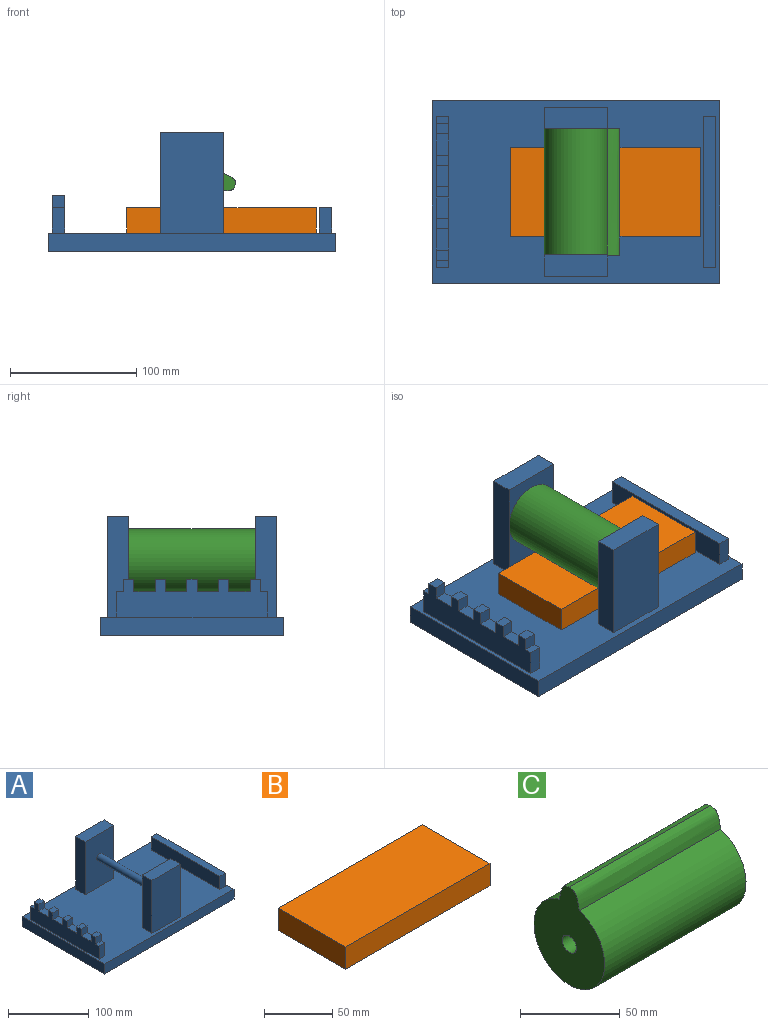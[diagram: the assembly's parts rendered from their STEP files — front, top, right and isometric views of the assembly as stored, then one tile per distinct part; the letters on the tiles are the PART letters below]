
ASSEMBLY  parts=3 mates=2
PART A: 47 faces, bbox 227.5x144.3x95 mm
  f0: plane 17x10mm, normal (0,0,1), area 170mm2, adj f17,f19,f41,f45
  f1: plane 17x10mm, normal (0,0,1), area 170mm2, adj f17,f19,f38,f42
  f2: plane 17x10mm, normal (0,0,1), area 170mm2, adj f17,f19,f35,f39
  f3: plane 17x10mm, normal (0,0,1), area 170mm2, adj f17,f19,f32,f36
  f4: plane 10x6mm, normal (0,0,1), area 60mm2, adj f16,f17,f19,f33
  f5: plane 227.5x144.3mm, normal (0,0,1), area 28729mm2, adj f6,f7,f8,f9,f11,f12,f13,f14
  f6: plane 144.3x15mm, normal (1,0,0), area 2164.5mm2, adj f5,f7,f9,f10
  f7: plane 227.5x15mm, normal (0,-1,0), area 3412.5mm2, adj f5,f6,f8,f10
  f8: plane 144.3x15mm, normal (-1,0,0), area 2164.5mm2, adj f5,f7,f9,f10
  f9: plane 227.5x15mm, normal (0,1,0), area 3412.5mm2, adj f5,f6,f8,f10
  f10: plane 227.5x144.3mm, normal (0,0,-1), area 32829mm2, adj f6,f7,f8,f9
  f11: plane 20x10mm, normal (0,-1,0), area 200mm2, adj f5,f12,f14,f15
  f12: plane 120x20mm, normal (1,0,0), area 2400mm2, adj f5,f11,f13,f15
  f13: plane 20x10mm, normal (0,1,0), area 200mm2, adj f5,f12,f14,f15
  f14: plane 120x20mm, normal (-1,0,0), area 2400mm2, adj f5,f11,f13,f15
  f15: plane 120x10mm, normal (0,0,1), area 1200mm2, adj f11,f12,f13,f14
  f16: plane 20x10mm, normal (0,1,0), area 200mm2, adj f4,f5,f17,f19
  f17: plane 120x30mm, normal (-1,0,0), area 2800mm2, adj f0,f1,f2,f3,f4,f5,f16,f18
  f18: plane 20x10mm, normal (0,-1,0), area 200mm2, adj f5,f17,f19,f20
  f19: plane 120x30mm, normal (1,0,0), area 2800mm2, adj f0,f1,f2,f3,f4,f5,f16,f18
  f20: plane 10x6mm, normal (0,0,1), area 60mm2, adj f17,f18,f19,f44
  f21: plane 80x50mm, normal (0,1,0), area 4000mm2, adj f5,f22,f24,f25
  f22: plane 80x17mm, normal (-1,0,0), area 1360mm2, adj f5,f21,f23,f25
  f23: plane 80x50mm, normal (0,-1,0), area 3921.5mm2, adj f5,f22,f24,f25,f26
  f24: plane 80x17mm, normal (1,0,0), area 1360mm2, adj f5,f21,f23,f25
  f25: plane 50x17mm, normal (0,0,1), area 850mm2, adj f21,f22,f23,f24
  f26: cylinder r=5mm len=100mm, axis (0,-1,0), area 3141.6mm2, adj f23,f30
  f27: plane 80x17mm, normal (-1,0,0), area 1360mm2, adj f5,f28,f30,f31
  f28: plane 80x50mm, normal (0,-1,0), area 4000mm2, adj f5,f27,f29,f31
  f29: plane 80x17mm, normal (1,0,0), area 1360mm2, adj f5,f28,f30,f31
  f30: plane 80x50mm, normal (0,1,0), area 3921.5mm2, adj f5,f26,f27,f29,f31
  f31: plane 50x17mm, normal (0,0,1), area 850mm2, adj f27,f28,f29,f30
  f32: plane 10x10mm, normal (0,-1,0), area 100mm2, adj f3,f17,f19,f34
  f33: plane 10x10mm, normal (0,1,0), area 100mm2, adj f4,f17,f19,f34
  f34: plane 10x8mm, normal (0,0,1), area 80mm2, adj f17,f19,f32,f33
  f35: plane 10x10mm, normal (0,-1,0), area 100mm2, adj f2,f17,f19,f37
  f36: plane 10x10mm, normal (0,1,0), area 100mm2, adj f3,f17,f19,f37
  f37: plane 10x8mm, normal (0,0,1), area 80mm2, adj f17,f19,f35,f36
  f38: plane 10x10mm, normal (0,-1,0), area 100mm2, adj f1,f17,f19,f40
  f39: plane 10x10mm, normal (0,1,0), area 100mm2, adj f2,f17,f19,f40
  f40: plane 10x8mm, normal (0,0,1), area 80mm2, adj f17,f19,f38,f39
  f41: plane 10x10mm, normal (0,-1,0), area 100mm2, adj f0,f17,f19,f43
  f42: plane 10x10mm, normal (0,1,0), area 100mm2, adj f1,f17,f19,f43
  f43: plane 10x8mm, normal (0,0,1), area 80mm2, adj f17,f19,f41,f42
  f44: plane 10x10mm, normal (0,-1,0), area 100mm2, adj f17,f19,f20,f46
  f45: plane 10x10mm, normal (0,1,0), area 100mm2, adj f0,f17,f19,f46
  f46: plane 10x8mm, normal (0,0,1), area 80mm2, adj f17,f19,f44,f45
PART B: 6 faces, bbox 150x70x20 mm
  f0: plane 70x20mm, normal (1,0,0), area 1400mm2, adj f1,f3,f4,f5
  f1: plane 150x20mm, normal (0,1,0), area 3000mm2, adj f0,f2,f4,f5
  f2: plane 70x20mm, normal (-1,0,0), area 1400mm2, adj f1,f3,f4,f5
  f3: plane 150x20mm, normal (0,-1,0), area 3000mm2, adj f0,f2,f4,f5
  f4: plane 150x70mm, normal (0,0,1), area 10500mm2, adj f0,f1,f2,f3
  f5: plane 150x70mm, normal (0,0,-1), area 10500mm2, adj f0,f1,f2,f3
PART C: 6 faces, bbox 100x50x60 mm
  f0: cylinder r=25mm len=100mm, axis (-1,0,0), area 14287.1mm2, adj f1,f2,f3,f4
  f1: extruded ~100x11mm, area 1441.6mm2, adj f0,f2,f3,f4
  f2: extruded ~100x11mm, area 1441.6mm2, adj f0,f1,f3,f4
  f3: plane 60x50mm, normal (1,0,0), area 1995.6mm2, adj f0,f1,f2,f5
  f4: plane 60x50mm, normal (-1,0,0), area 1995.6mm2, adj f0,f1,f2,f5
  f5: cylinder r=5mm len=100mm, axis (-1,0,0), area 3141.6mm2, adj f3,f4
PLACE A at identity fixed
PLACE B t=(23.33,0,0)mm
PLACE C rot(axis=(0.61,0.61,0.5),126.7deg) t=(0,0,45)mm
MATE slider B.f0 <-> A.f14  axis (1,0,0) through (98.33,0,10)mm
MATE revolute C.f0 <-> A.f26  axis (0,-1,0) through (0,-50,45)mm
